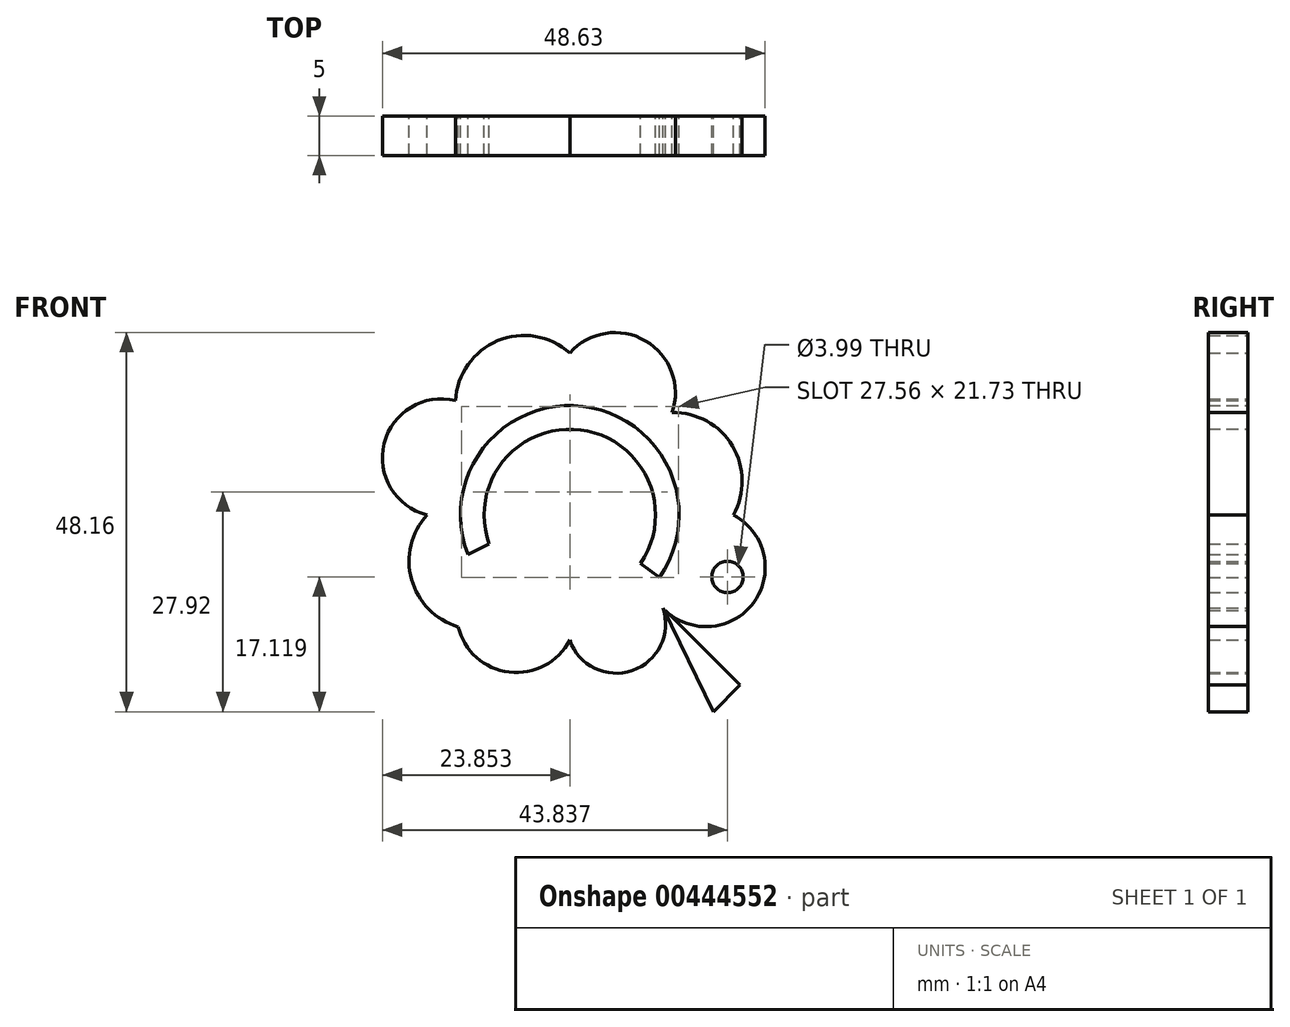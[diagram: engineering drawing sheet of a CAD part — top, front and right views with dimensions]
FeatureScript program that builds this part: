
annotation { "Feature Type Name" : "Feature", "Feature Type Description" : "" }
export const myFeature = defineFeature(function(context is Context, id is Id, definition is map)
    precondition{}
    {
        {
            var Q0;
            Q0=qCreatedBy(makeId("Front.planeOp"),FACE);
            var sketch = newSketch(context, id + "F0", { "sketchPlane" : qUnion([Q0])});
            skPoint(sketch, "E0.middle", {"position": v(0, 0) * mm});
            skArc(sketch, "E1", {"start": v(0, 20.57) * mm, "mid": v(-9.17, 22.12) * mm, "end": v(-14.5, 14.5) * mm});
            skArc(sketch, "E2", {"start": v(-14.5, 14.5) * mm, "mid": v(-23.58, 9.07) * mm, "end": v(-18.15, 0) * mm});
            skArc(sketch, "E3", {"start": v(20.76, 0) * mm, "mid": v(20.66, 8.76) * mm, "end": v(13, 13) * mm});
            skArc(sketch, "E4", {"start": v(13, 13) * mm, "mid": v(9.6, 22.12) * mm, "end": v(0, 20.57) * mm});
            skArc(sketch, "E5", {"start": v(11.84, -11.84) * mm, "mid": v(23.3, -11.2) * mm, "end": v(20.76, 0) * mm});
            skArc(sketch, "E6", {"start": v(-18.15, 0) * mm, "mid": v(-20.1, -8.2) * mm, "end": v(-14.2, -14.2) * mm});
            skArc(sketch, "E7", {"start": v(-14.2, -14.2) * mm, "mid": v(-7.7, -19.97) * mm, "end": v(0, -15.9) * mm});
            skArc(sketch, "E8", {"start": v(0, -15.9) * mm, "mid": v(7.95, -19.78) * mm, "end": v(11.84, -11.84) * mm});
            skLineSegment(sketch, "E9", {"start": v(11.84, -11.84) * mm, "end": v(18.22, -25) * mm});
            skLineSegment(sketch, "E10", {"start": v(18.22, -25) * mm, "end": v(21.61, -21.61) * mm});
            skLineSegment(sketch, "E11", {"start": v(21.61, -21.61) * mm, "end": v(11.84, -11.84) * mm});
            skArc(sketch, "E12", {"start": v(8.99, -6.14) * mm, "mid": v(1.37, 10.8) * mm, "end": v(-10.24, -3.7) * mm});
            skArc(sketch, "E13.0", {"start": v(11.39, -7.95) * mm, "mid": v(1.67, 13.79) * mm, "end": v(-12.95, -5) * mm});
            skLineSegment(sketch, "E14", {"start": v(11.39, -7.95) * mm, "end": v(8.99, -6.14) * mm});
            skLineSegment(sketch, "E15", {"start": v(-10.24, -3.7) * mm, "end": v(-12.95, -5) * mm});
            skCircle(sketch, "E16", {"center": v(20.03, -7.88) * mm, "radius": 2 * mm});
            skSolve(sketch);
        }
        {
            var Q0;
            {var subQ1=sQuery(id+"F0.wireOp",EDGE,"E9");Q0=makeQuery(id+"F0.imprint","IMPRINT",FACE,{"disambiguationData":[TD([[makeQuery(id+"F0.imprint","IMPRINT",EDGE,{"derivedFrom":subQ1}),1.0]])]});}
            var Q1;
            Q1=makeQuery(id+"F0.imprint","IMPRINT",FACE,{"disambiguationData":[TD([[makeQuery(id+"F0.imprint","IMPRINT",EDGE,{"derivedFrom":sQuery(id+"F0.wireOp",EDGE,"E1")}),1.0]])]});
            var Q2;
            {var subQ0=sQuery(id+"F0.wireOp",EDGE,"E11");var subQ1=sQuery(id+"F0.wireOp",EDGE,"E5");var subQ3=makeQuery(id+"F0.imprint","INTERSECT",VERTEX,{"derivedFrom":[subQ1,subQ0]});Q2=makeQuery(id+"F0.imprint","IMPRINT",FACE,{"disambiguationData":[TD([[makeQuery(id+"F0.imprint","IMPRINT",EDGE,{"disambiguationData":[TD([[subQ3,1.0]])],"derivedFrom":subQ1}),1.0]])]});}
            var Q3;
            Q3 = qSketchRegion(id + "F0", true);
            extrude(context, id + "F1", {"entities" : qUnion([Q0, Q1, Q2, Q3]), "depth" : 5 * mm});
        }
    });
